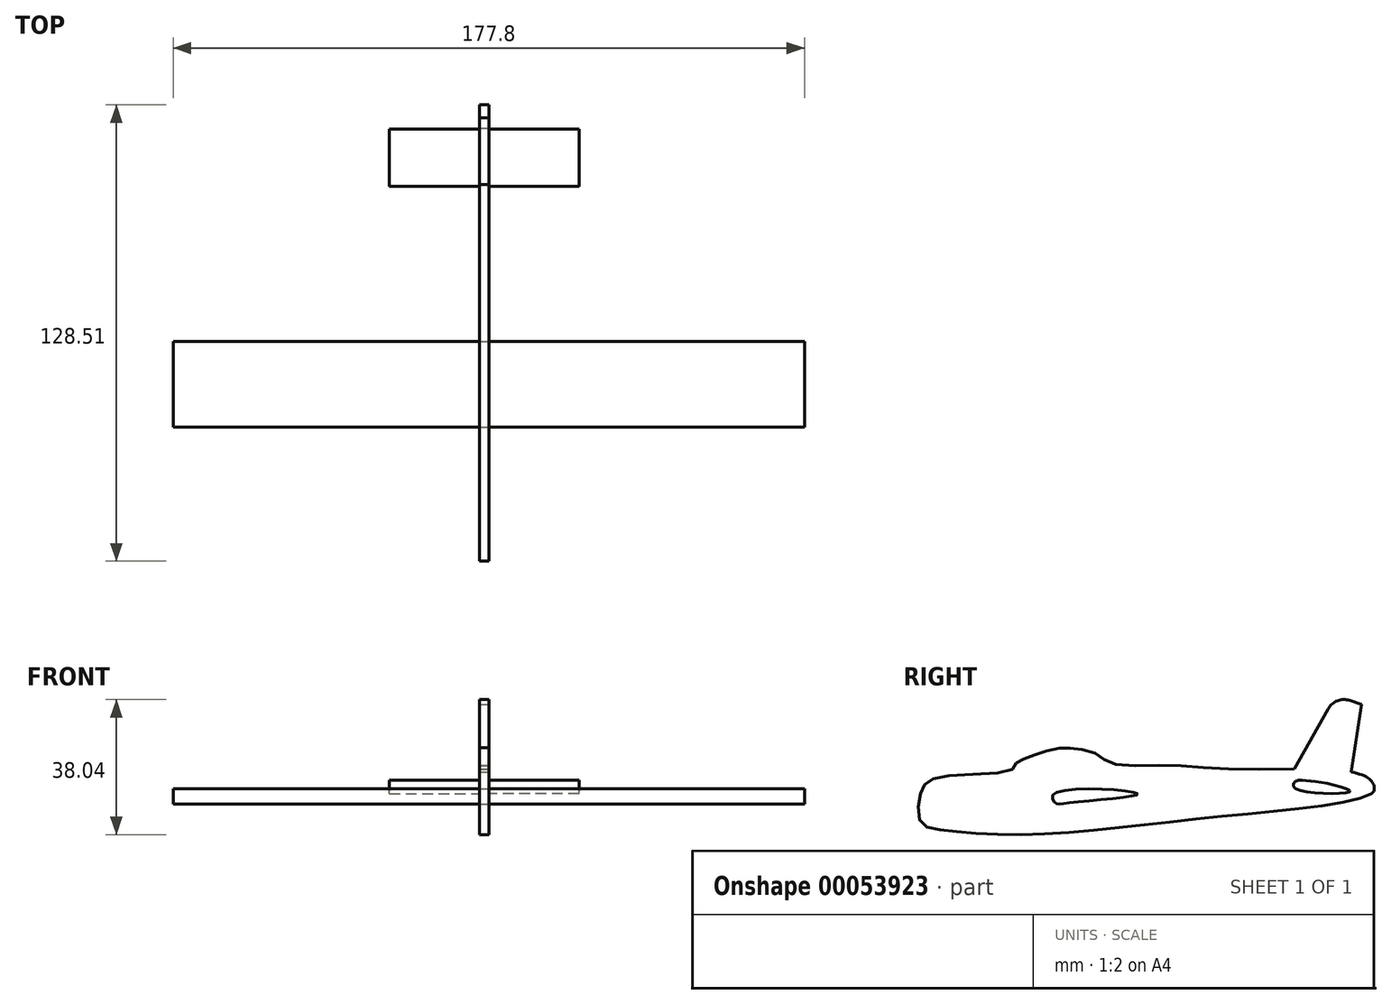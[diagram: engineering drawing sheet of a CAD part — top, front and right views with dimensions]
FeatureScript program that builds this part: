
annotation { "Feature Type Name" : "Feature", "Feature Type Description" : "" }
export const myFeature = defineFeature(function(context is Context, id is Id, definition is map)
    precondition{}
    {
        {
            var Q0;
            Q0=qCreatedBy(makeId("Right.planeOp"),FACE);
            var sketch = newSketch(context, id + "F0", { "sketchPlane" : qUnion([Q0])});
            skLineSegment(sketch, "E0", {"start": v(-53.5, 0) * mm, "end": v(73.5, 0) * mm});
            skFitSpline(sketch, "E1", {"points": [v(-53.5, 0) * mm, v(-51.8, 3.05) * mm, v(-44.95, 5.2) * mm, v(-27.81, 6.7) * mm, v(-26.74, 8.4) * mm, v(-24.6, 9.7) * mm, v(-19.89, 11.4) * mm, v(-14.1, 12.9) * mm, v(-9.82, 12.7) * mm, v(-3.82, 11.2) * mm, v(0, 8.62) * mm, v(15.67, 7.98) * mm, v(36.66, 6.9) * mm, v(71.14, 5.2) * mm, v(74.35, 1.77) * mm, v(73.5, 0) * mm, v(61.07, -3.16) * mm, v(31.52, -6.37) * mm, v(0, -9.8) * mm, v(-28.24, -11.51) * mm, v(-47.3, -10.23) * mm, v(-53.5, -7.87) * mm, v(-53.5, 0) * mm]});
            skLineSegment(sketch, "E2", {"start": v(51.86, 6.95) * mm, "end": v(63.43, 27.63) * mm});
            skLineSegment(sketch, "E3", {"start": v(63.43, 27.63) * mm, "end": v(70.71, 25.11) * mm});
            skLineSegment(sketch, "E4", {"start": v(70.71, 25.11) * mm, "end": v(67.84, 6.08) * mm});
            skSolve(sketch);
        }
        {
            var Q0;
            {var subQ0=sQuery(id+"F0.wireOp",EDGE,"E0");Q0=makeQuery(id+"F0.imprint","IMPRINT",FACE,{"disambiguationData":[TD([[makeQuery(id+"F0.imprint","IMPRINT",EDGE,{"derivedFrom":subQ0}),-1.0]])]});}
            var Q1;
            {var subQ0=sQuery(id+"F0.wireOp",EDGE,"E0");Q1=makeQuery(id+"F0.imprint","IMPRINT",FACE,{"disambiguationData":[TD([[makeQuery(id+"F0.imprint","IMPRINT",EDGE,{"derivedFrom":subQ0}),1.0]])]});}
            var Q2;
            {var subQ0=sQuery(id+"F0.wireOp",EDGE,"E2");Q2=makeQuery(id+"F0.imprint","IMPRINT",FACE,{"disambiguationData":[TD([[makeQuery(id+"F0.imprint","IMPRINT",EDGE,{"derivedFrom":subQ0}),-1.0]])]});}
            extrude(context, id + "F1", {"entities" : qUnion([Q0, Q1, Q2]), "endBound" : BoundingType.SYMMETRIC, "depth" : 2.54 * mm});
        }
        {
            var Q0;
            Q0=makeQuery(id+"F1.opExtrude","CAP_FACE",FACE,{"disambiguationData":[OSD([sQuery(id+"F0.wireOp",EDGE,"E1"),sQuery(id+"F0.wireOp",EDGE,"E2"),sQuery(id+"F0.wireOp",EDGE,"E3"),sQuery(id+"F0.wireOp",EDGE,"E4")])],"isStart":false});
            var sketch = newSketch(context, id + "F2", { "sketchPlane" : qUnion([Q0])});
            skFitSpline(sketch, "E5", {"points": [v(-11.48, -2.56) * mm, v(-15.53, -2.56) * mm, v(-15.8, 0) * mm, v(7.67, 0) * mm, v(-11.48, -2.56) * mm]});
            skSolve(sketch);
        }
        {
            var Q0;
            Q0 = qSketchRegion(id + "F2", true);
            extrude(context, id + "F3", {"entities" : qUnion([Q0]), "endBound" : BoundingType.SYMMETRIC, "depth" : 177.8 * mm});
        }
        {
            var Q0;
            Q0=makeQuery(id+"F3.opExtrude","SWEPT_BODY",BODY,{"disambiguationData":[OSD([sQuery(id+"F2.wireOp",EDGE,"E5")])]});
            var Q1;
            Q1=makeQuery(id+"F1.opExtrude","SWEPT_BODY",BODY,{"disambiguationData":[OSD([sQuery(id+"F0.wireOp",EDGE,"E1"),sQuery(id+"F0.wireOp",EDGE,"E2"),sQuery(id+"F0.wireOp",EDGE,"E3"),sQuery(id+"F0.wireOp",EDGE,"E4")])]});
            booleanBodies(context, id + "F4", {"operationType" : BooleanOperationType.SUBTRACTION, "tools" : qUnion([Q0]), "targets" : qUnion([Q1]), "keepTools" : true});
        }
        {
            var Q0;
            Q0=makeQuery(id+"F1.opExtrude","CAP_FACE",FACE,{"disambiguationData":[OSD([sQuery(id+"F0.wireOp",EDGE,"E1"),sQuery(id+"F0.wireOp",EDGE,"E2"),sQuery(id+"F0.wireOp",EDGE,"E3"),sQuery(id+"F0.wireOp",EDGE,"E4")])],"isStart":false});
            var sketch = newSketch(context, id + "F5", { "sketchPlane" : qUnion([Q0])});
            skFitSpline(sketch, "E6", {"points": [v(51.54, 2.1) * mm, v(52.12, 3.5) * mm, v(55.13, 3.72) * mm, v(61.6, 2.8) * mm, v(67.5, 0.71) * mm, v(59.4, 0.13) * mm, v(51.54, 2.1) * mm]});
            skSolve(sketch);
        }
        {
            var Q0;
            Q0=makeQuery(id+"F5.imprint","IMPRINT",FACE,{"disambiguationData":[TD([[makeQuery(id+"F5.imprint","IMPRINT",EDGE,{"derivedFrom":sQuery(id+"F5.wireOp",EDGE,"E6")}),-1.0]])]});
            extrude(context, id + "F6", {"entities" : qUnion([Q0]), "operationType" : NewBodyOperationType.ADD, "depth" : 25.4 * mm});
        }
        {
            var Q0;
            Q0=makeQuery(id+"F1.opExtrude","SWEPT_EDGE",EDGE,{"disambiguationData":[OSD([sQuery(id+"F0.wireOp",EDGE,"E2"),sQuery(id+"F0.wireOp",EDGE,"E3")])]});
            fillet(context, id + "F7", {"entities" : qUnion([Q0]), "radius" : 5.08 * mm, "tangentPropagation" : true, "allowEdgeOverflow" : false});
        }
        {
            var Q0;
            Q0=makeQuery(id+"F1.opExtrude","SWEPT_BODY",BODY,{"disambiguationData":[OSD([sQuery(id+"F0.wireOp",EDGE,"E1"),sQuery(id+"F0.wireOp",EDGE,"E2"),sQuery(id+"F0.wireOp",EDGE,"E3"),sQuery(id+"F0.wireOp",EDGE,"E4")])]});
            var Q1;
            Q1=qCreatedBy(makeId("Right.planeOp"),FACE);
            mirror(context, id + "F8", {"entities" : qUnion([Q0]), "mirrorPlane" : qUnion([Q1])});
        }
    });
